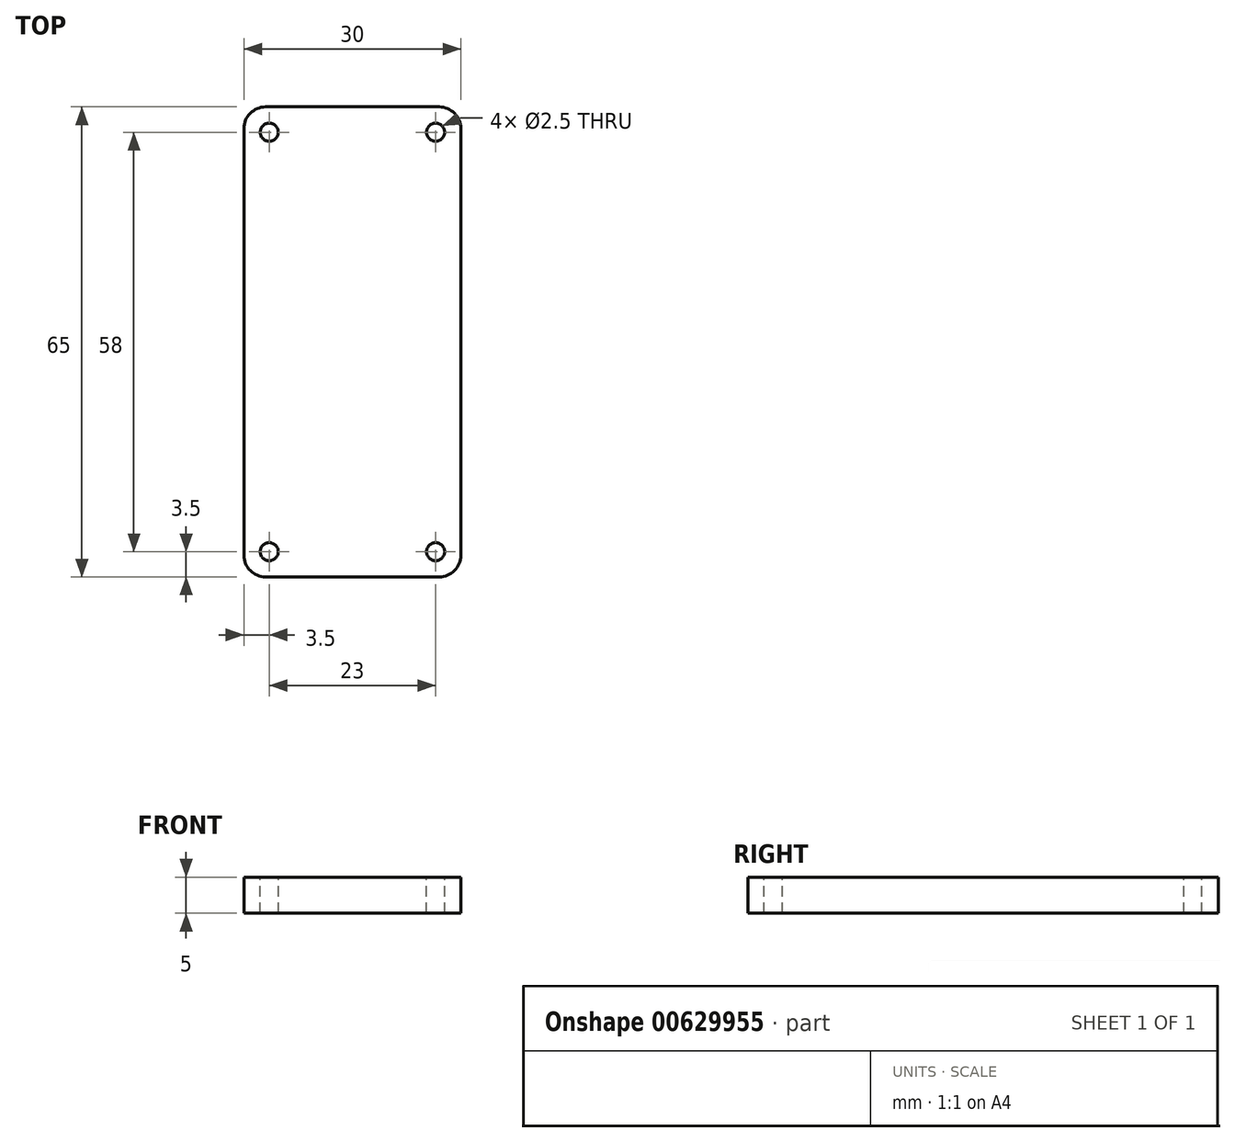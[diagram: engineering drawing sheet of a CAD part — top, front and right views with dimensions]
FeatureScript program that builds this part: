
annotation { "Feature Type Name" : "Feature", "Feature Type Description" : "" }
export const myFeature = defineFeature(function(context is Context, id is Id, definition is map)
    precondition{}
    {
        {
            var Q0;
            Q0=qCreatedBy(makeId("Top.planeOp"),FACE);
            var sketch = newSketch(context, id + "F0", { "sketchPlane" : qUnion([Q0])});
            skLineSegment(sketch, "E0.bottom", {"start": v(-15, 32.5) * mm, "end": v(15, 32.5) * mm});
            skLineSegment(sketch, "E0.top", {"start": v(-15, -32.5) * mm, "end": v(15, -32.5) * mm});
            skLineSegment(sketch, "E0.left", {"start": v(-15, 32.5) * mm, "end": v(-15, -32.5) * mm});
            skLineSegment(sketch, "E0.right", {"start": v(15, 32.5) * mm, "end": v(15, -32.5) * mm});
            skPoint(sketch, "E0.middle", {"position": v(0, 0) * mm});
            skSolve(sketch);
        }
        {
            var Q0;
            Q0 = qSketchRegion(id + "F0", true);
            extrude(context, id + "F1", {"entities" : qUnion([Q0]), "depth" : 5 * mm, "offsetDistance" : 25.4 * mm});
        }
        {
            var Q0;
            Q0=makeQuery(id+"F1.opExtrude","SWEPT_EDGE",EDGE,{"disambiguationData":[OSD([sQuery(id+"F0.wireOp",EDGE,"E0.top"),sQuery(id+"F0.wireOp",EDGE,"E0.right")])]});
            var Q1;
            Q1=makeQuery(id+"F1.opExtrude","SWEPT_EDGE",EDGE,{"disambiguationData":[OSD([sQuery(id+"F0.wireOp",EDGE,"E0.bottom"),sQuery(id+"F0.wireOp",EDGE,"E0.right")])]});
            var Q2;
            Q2=makeQuery(id+"F1.opExtrude","SWEPT_EDGE",EDGE,{"disambiguationData":[OSD([sQuery(id+"F0.wireOp",EDGE,"E0.top"),sQuery(id+"F0.wireOp",EDGE,"E0.left")])]});
            var Q3;
            Q3=makeQuery(id+"F1.opExtrude","SWEPT_EDGE",EDGE,{"disambiguationData":[OSD([sQuery(id+"F0.wireOp",EDGE,"E0.bottom"),sQuery(id+"F0.wireOp",EDGE,"E0.left")])]});
            fillet(context, id + "F2", {"entities" : qUnion([Q0, Q1, Q2, Q3]), "radius" : 3 * mm, "tangentPropagation" : true, "allowEdgeOverflow" : false});
        }
        {
            var Q0;
            Q0=makeQuery(id+"F1.opExtrude","CAP_FACE",FACE,{"disambiguationData":[OSD([sQuery(id+"F0.wireOp",EDGE,"E0.bottom"),sQuery(id+"F0.wireOp",EDGE,"E0.top"),sQuery(id+"F0.wireOp",EDGE,"E0.left"),sQuery(id+"F0.wireOp",EDGE,"E0.right")])],"isStart":false});
            var sketch = newSketch(context, id + "F3", { "sketchPlane" : qUnion([Q0])});
            skPoint(sketch, "E1", {"position": v(-11.5, -29) * mm});
            skPoint(sketch, "E2", {"position": v(-11.5, 29) * mm});
            skPoint(sketch, "E3", {"position": v(11.5, 29) * mm});
            skPoint(sketch, "E4", {"position": v(11.5, -29) * mm});
            skSolve(sketch);
        }
        {
            var Q0;
            Q0=sQuery(id+"F3.wireOp",VERTEX,"E1");
            var Q1;
            Q1=sQuery(id+"F3.wireOp",VERTEX,"E4");
            var Q2;
            Q2=sQuery(id+"F3.wireOp",VERTEX,"E3");
            var Q3;
            Q3=sQuery(id+"F3.wireOp",VERTEX,"E2");
            var Q4;
            Q4=makeQuery(id+"F1.opExtrude","SWEPT_BODY",BODY,{"disambiguationData":[OSD([sQuery(id+"F0.wireOp",EDGE,"E0.bottom"),sQuery(id+"F0.wireOp",EDGE,"E0.top"),sQuery(id+"F0.wireOp",EDGE,"E0.left"),sQuery(id+"F0.wireOp",EDGE,"E0.right")])]});
            hole(context, id + "F4", {"style" : HoleStyle.SIMPLE, "endStyle" : HoleEndStyle.THROUGH, "holeDiameter" : 2.5 * mm, "majorDiameter" : 6.35 * mm, "isTappedThrough" : true, "tappedDepth" : 12.7 * mm, "tapClearance" : 3, "locations" : qUnion([Q0, Q1, Q2, Q3]), "scope" : qUnion([Q4])});
        }
    });
